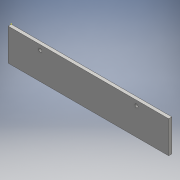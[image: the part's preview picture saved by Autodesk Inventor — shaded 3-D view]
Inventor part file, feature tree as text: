
AUTODESK INVENTOR PART (.ipt)
format: ipt  version: 2016 (Build 200138000, 138)  size: 101,376 bytes
history: native  units: mm
features: sketch x3, extrude x2
ambient origin geometry x8: Origin, YZ Plane, XZ Plane, XY Plane, X Axis, Y Axis, Z Axis, Center Point
bodies: Solid1 (feature_tree)
feature tree (5):
  extrude  "Extrusion1"  Depth=100.0mm
  sketch  "Sketch2"  dims[d3=10.0mm d4=0.0mm d5=10.0mm]
  extrude  "Extrusion2"  Depth=10.0mm
  sketch  "Sketch1"  dims[d0=500.0mm d1=100.0mm]
  sketch  "Sketch3"  dims[d6=10.0mm d7=15.0mm d8=15.0mm d9=100.0mm d10=100.0mm d11=10.0mm d12=0.0mm]
